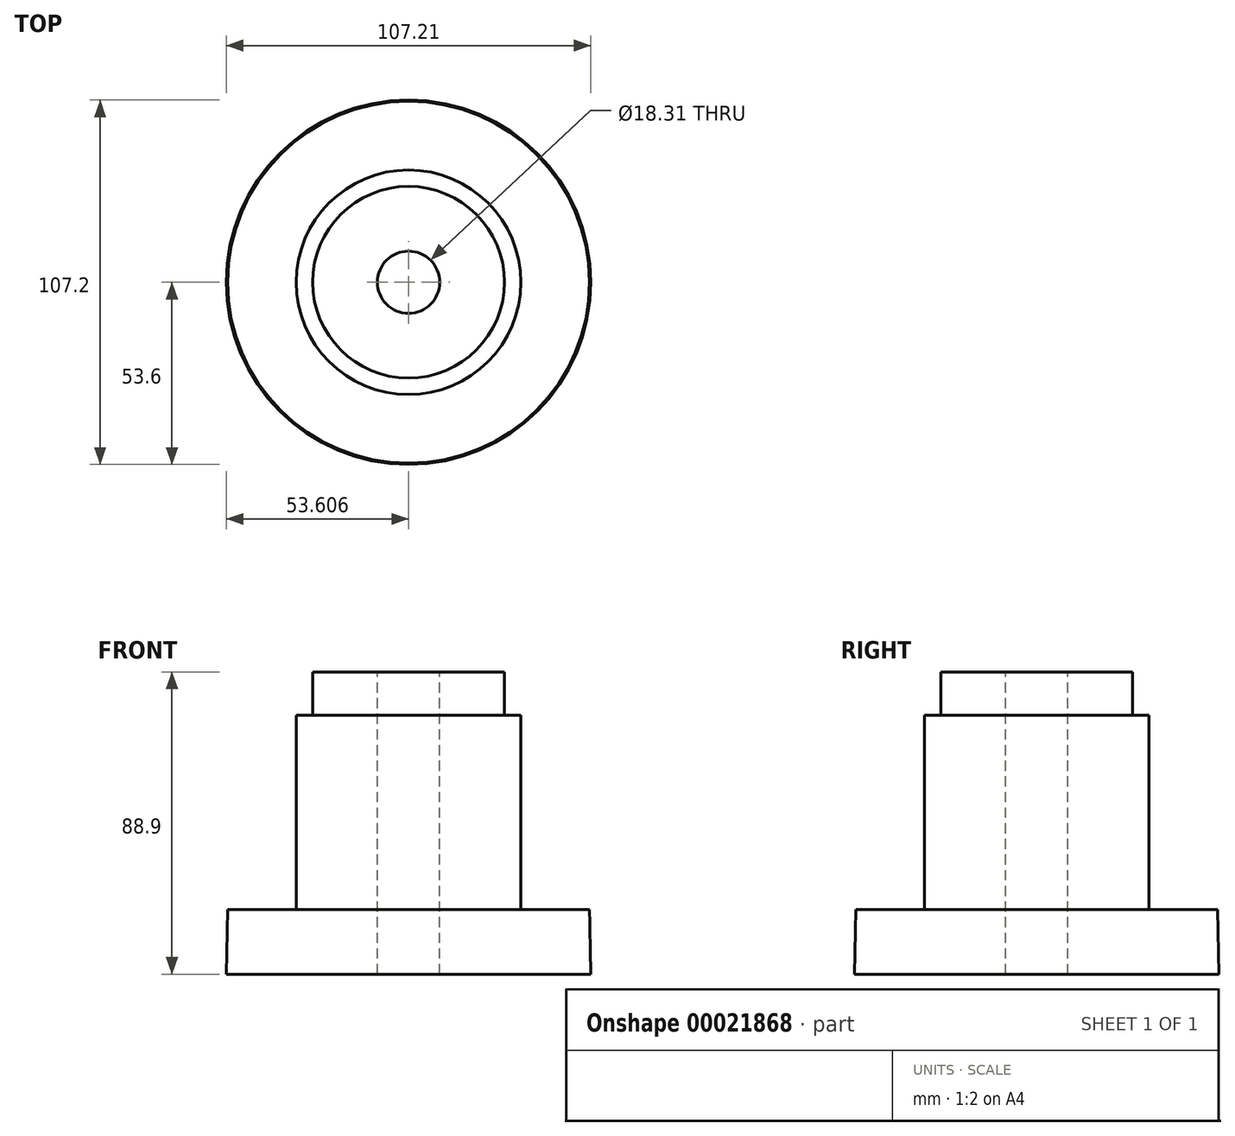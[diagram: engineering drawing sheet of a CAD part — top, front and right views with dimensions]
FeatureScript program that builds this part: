
annotation { "Feature Type Name" : "Feature", "Feature Type Description" : "" }
export const myFeature = defineFeature(function(context is Context, id is Id, definition is map)
    precondition{}
    {
        {
            var Q0;
            Q0=qCreatedBy(makeId("Front.planeOp"),FACE);
            var sketch = newSketch(context, id + "F0", { "sketchPlane" : qUnion([Q0])});
            skLineSegment(sketch, "E0", {"start": v(0, 0) * mm, "end": v(0, 88.9) * mm});
            skLineSegment(sketch, "E1", {"start": v(0, 88.9) * mm, "end": v(19.05, 88.9) * mm});
            skLineSegment(sketch, "E2", {"start": v(19.05, 88.9) * mm, "end": v(19.05, 76.2) * mm});
            skLineSegment(sketch, "E3", {"start": v(19.05, 76.2) * mm, "end": v(23.88, 76.2) * mm});
            skLineSegment(sketch, "E4", {"start": v(23.88, 76.2) * mm, "end": v(23.88, 19.05) * mm});
            skLineSegment(sketch, "E5", {"start": v(0, 0) * mm, "end": v(44.45, 0) * mm});
            skLineSegment(sketch, "E6", {"start": v(23.88, 19.05) * mm, "end": v(44.08, 19.05) * mm});
            skLineSegment(sketch, "E7", {"start": v(44.08, 19.05) * mm, "end": v(44.45, 0) * mm});
            skLineSegment(sketch, "E8", {"start": v(-9.15, 85.85) * mm, "end": v(-9.15, -2.63) * mm});
            skSolve(sketch);
        }
        {
            var Q0;
            Q0 = qSketchRegion(id + "F0", true);
            var Q1;
            Q1=sQuery(id+"F0.wireOp",EDGE,"E8");
            revolve(context, id + "F1", {"entities" : qUnion([Q0]), "axis" : qUnion([Q1]), "revolveType" : RevolveType.FULL});
        }
    });
